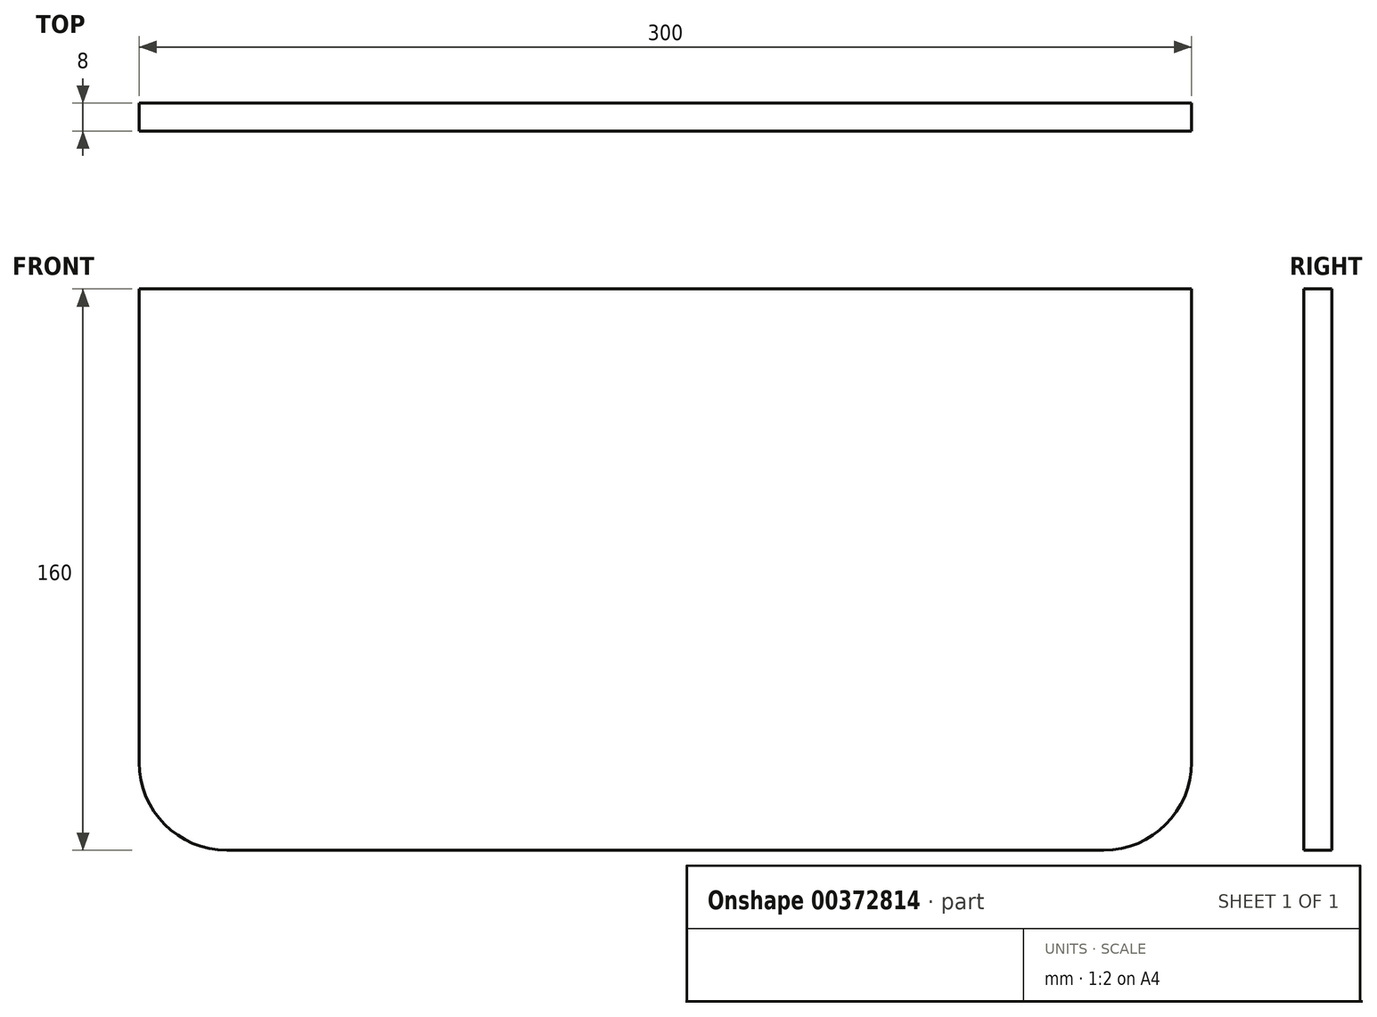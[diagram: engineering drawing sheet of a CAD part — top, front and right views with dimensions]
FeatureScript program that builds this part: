
annotation { "Feature Type Name" : "Feature", "Feature Type Description" : "" }
export const myFeature = defineFeature(function(context is Context, id is Id, definition is map)
    precondition{}
    {
        {
            var Q0;
            Q0=qCreatedBy(makeId("Front.planeOp"),FACE);
            var sketch = newSketch(context, id + "F0", { "sketchPlane" : qUnion([Q0])});
            skLineSegment(sketch, "E0.bottom", {"start": v(150, -80) * mm, "end": v(-150, -80) * mm});
            skLineSegment(sketch, "E0.top", {"start": v(150, 80) * mm, "end": v(-150, 80) * mm});
            skLineSegment(sketch, "E0.left", {"start": v(150, -80) * mm, "end": v(150, 80) * mm});
            skLineSegment(sketch, "E0.right", {"start": v(-150, -80) * mm, "end": v(-150, 80) * mm});
            skPoint(sketch, "E0.middle", {"position": v(0, 0) * mm});
            skSolve(sketch);
        }
        {
            var Q0;
            Q0 = qSketchRegion(id + "F0", true);
            extrude(context, id + "F1", {"entities" : qUnion([Q0]), "endBound" : BoundingType.SYMMETRIC, "depth" : 8 * mm});
        }
        {
            var Q0;
            Q0=makeQuery(id+"F1.opExtrude","SWEPT_EDGE",EDGE,{"disambiguationData":[OSD([sQuery(id+"F0.wireOp",EDGE,"E0.bottom"),sQuery(id+"F0.wireOp",EDGE,"E0.left")])]});
            var Q1;
            Q1=makeQuery(id+"F1.opExtrude","SWEPT_EDGE",EDGE,{"disambiguationData":[OSD([sQuery(id+"F0.wireOp",EDGE,"E0.bottom"),sQuery(id+"F0.wireOp",EDGE,"E0.right")])]});
            fillet(context, id + "F2", {"entities" : qUnion([Q0, Q1]), "radius" : 25 * mm, "tangentPropagation" : true, "allowEdgeOverflow" : false});
        }
    });
